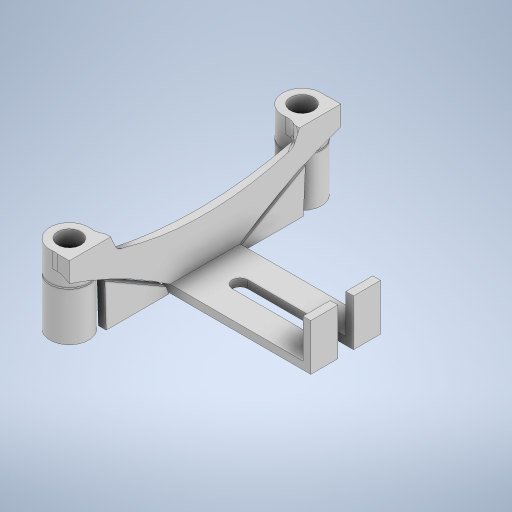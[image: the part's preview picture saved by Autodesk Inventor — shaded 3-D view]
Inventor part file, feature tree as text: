
AUTODESK INVENTOR PART (.ipt)
format: ipt  version: 2023 (Build 270158000, 158)  size: 660,480 bytes
history: native  units: in
note: dims shown in document units (in); Inventor stores cm internally (conversion verified against a paired STEP export)
features: sketch x12, extrude x9, plane x6, loft x3, fillet x3, mirror x1
ambient origin geometry x8: Origin, YZ Plane, XZ Plane, XY Plane, X Axis, Y Axis, Z Axis, Center Point
bodies: Solid1 (feature_tree)
feature tree (34):
  extrude  "Extrusion1"  Depth=0.2362in
  plane  "Work Plane1"
  extrude  "Extrusion2"  Depth=1.1811in
  plane  "Work Plane2"
  sketch  "Sketch4"  dims[d6=0.3937in d7=0.3937in]
  sketch  "Sketch5"  dims[d8=0.2953in d9=0.2953in]
  extrude  "Extrusion3"  Depth=0.3937in
  extrude  "Extrusion4"  Depth=0.2953in
  plane  "Work Plane3"
  loft  "Loft1"
  extrude  "Extrusion5"  [1 undecoded]
  fillet  "Fillet1"  Radius=0.0787in
  extrude  "Extrusion6"  Depth=0.5118in
  fillet  "Fillet3"  Radius=2.3622in
  fillet  "Fillet4"  Radius=1.1811in
  extrude  "Extrusion7"  Depth=0.0787in
  extrude  "Extrusion8"  Depth=0.0787in
  sketch  "Sketch14"  dims[d27=0.0787in d28=-0.0787in]
  plane  "Work Plane5"
  mirror  "Mirror1"
  sketch  "Sketch15"  dims[d32=2.9528in d33=0.0in d34=0.0in]
  loft  "Loft2"
  loft  "Loft3"
  extrude  "Extrusion9"  [1 undecoded]
  sketch  "Sketch2"  dims[d2=0.2362in d3=0.2362in]
  sketch  "Sketch3"  dims[d4=2.3622in d5=1.1811in]
  sketch  "Sketch6"  dims[d10=0.2953in d11=0.2953in]
  sketch  "Sketch7"  dims[d12=0.1575in d13=0.0in d14=-0.7972in d15=0.0787in]
  sketch  "Sketch9"  dims[d16=0.4331in d19=0.5118in d20=2.3622in d21=1.1811in]
  sketch  "Sketch11"  dims[d22=0.0787in d23=0.0in d24=0.0787in]
  sketch  "Sketch12"  dims[d25=0.0787in d26=0.0787in]
  plane  "Work Plane4"
  plane  "Work Plane6"
  sketch  "Sketch16"  dims[d35=0.0in d36=0.0in d37=-0.0787in d38=2.9528in d39=2.9528in d40=3.937in d41=0.0in d42=90.0deg d43=0.0in d44=90.0deg d45=0.1181in d46=0.2953in d47=0.2953in d48=0.1181in d49=0.3937in d50=0.0in d51=0.0787in d52=0.3937in d53=0.0in d55=0.0787in d56=0.0787in d57=0.9941in d58=0.0787in d59=0.0787in d60=0.3937in d61=0.0in d64=3.937in d66=0.7087in d67=0.2756in d68=0.1378in d69=0.0in d70=0.3937in d71=0.2559in d72=0.2559in d73=-0.2061in d74=-0.0472in d75=0.0in d76=90.0deg d77=0.0in d78=90.0deg d79=0.0in d80=90.0deg d81=0.0in d82=90.0deg d83=0.4882in d84=0.0in d85=3.937in]
note: 2 required parameter values undecoded (feature->parameter linkage not recoverable at this tier; creation-order binding heuristic only, values carry confidence <= 0.55)
